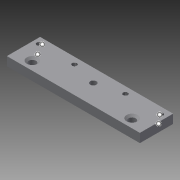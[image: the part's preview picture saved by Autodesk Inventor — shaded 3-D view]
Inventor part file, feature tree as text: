
AUTODESK INVENTOR PART (.ipt)
format: ipt  version: 2015 SP1 (Build 190203100, 203)  size: 109,568 bytes
history: native  units: mm
features: hole x6, pattern_linear x2, extrude x1, sketch x1
ambient origin geometry x8: Origin, YZ Plane, XZ Plane, XY Plane, X Axis, Y Axis, Z Axis, Center Point
bodies: Solid1 (feature_tree)
feature tree (10):
  extrude  "Extrusion1"  Depth=8.0mm TaperAngle=0.0deg
  hole  "Hole1"  [1 undecoded]
  hole  "Hole2"  [1 undecoded]
  hole  "Hole3"  [1 undecoded]
  hole  "Hole4"  [1 undecoded]
  hole  "Hole5"  [1 undecoded]
  hole  "Hole6"  [1 undecoded]
  pattern_linear  "Rectangular Pattern1"  Spacing1=0.0mm  [1 undecoded]
  pattern_linear  "Rectangular Pattern2"  Spacing1=6.0mm  [1 undecoded]
  sketch  "Sketch1"  dims[d1=30.0mm d2=8.0mm d3=0.0mm d4=15.0mm d5=8.0mm d6=6.5mm d7=6.0mm d8=10.0mm d9=2.0mm d10=90.0deg d11=8.0mm d12=20.594885mm d13=15.0mm d14=8.0mm d15=6.5mm d16=6.0mm d17=10.0mm d18=2.0mm d19=90.0deg d20=8.0mm d21=20.594885mm d22=60.0mm d23=12.0mm d24=16.0mm d25=10.0mm d26=10.0mm d27=2.0mm d28=90.0deg d29=5.0mm d30=0.0mm d31=10.0mm d32=10.0mm d33=5.5mm d34=16.0mm d35=10.0mm d36=2.0mm d37=90.0deg d38=22.2mm d39=20.594885mm d40=5.0mm d41=6.0mm d42=4.134mm d43=10.0mm d44=10.0mm d45=2.0mm d46=90.0deg d47=14.2mm d48=20.594885mm d49=0.0mm d50=0.0mm d51=6.0mm d52=5.0mm d53=4.134mm d54=10.0mm d55=10.0mm d56=2.0mm d57=90.0deg d58=14.2mm d59=20.594885mm d60=0.0mm d61=0.0mm d62=20.0mm d64=32.0mm d65=20.0mm d67=32.0mm]
note: 8 required parameter values undecoded (feature->parameter linkage not recoverable at this tier; creation-order binding heuristic only, values carry confidence <= 0.55)
